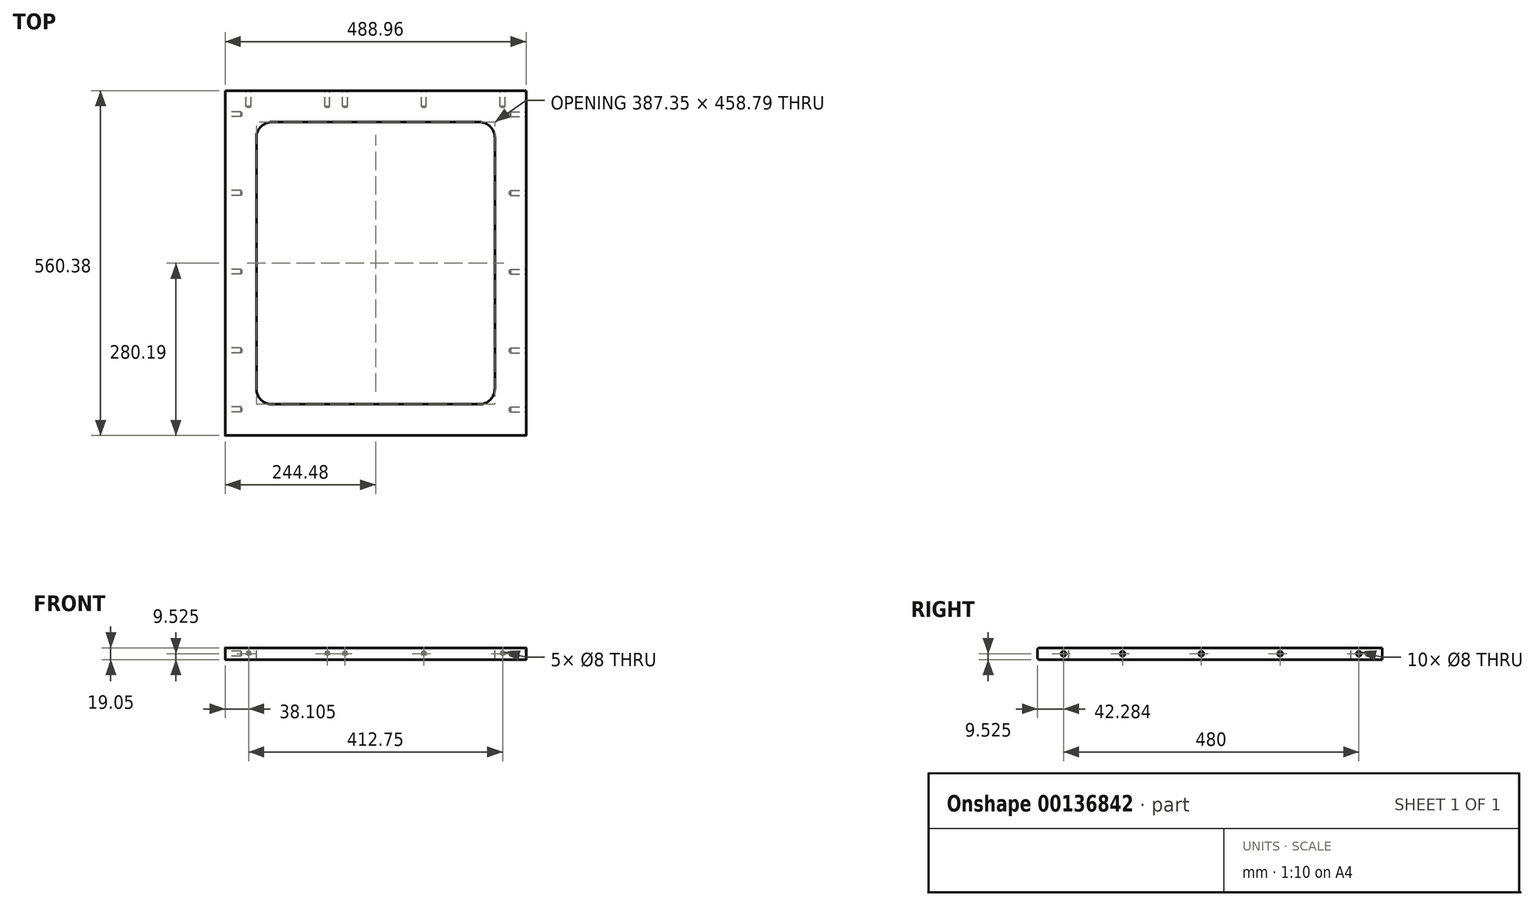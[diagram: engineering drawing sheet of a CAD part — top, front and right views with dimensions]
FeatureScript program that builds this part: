
annotation { "Feature Type Name" : "Feature", "Feature Type Description" : "" }
export const myFeature = defineFeature(function(context is Context, id is Id, definition is map)
    precondition{}
    {
        {
            var Q0;
            Q0=qCreatedBy(makeId("Top.planeOp"),FACE);
            var sketch = newSketch(context, id + "F0", { "sketchPlane" : qUnion([Q0])});
            skLineSegment(sketch, "E0.bottom", {"start": v(244.48, -280.2) * mm, "end": v(-244.47, -280.2) * mm});
            skLineSegment(sketch, "E0.top", {"start": v(244.47, 280.2) * mm, "end": v(-244.48, 280.2) * mm});
            skLineSegment(sketch, "E0.left", {"start": v(244.48, -280.2) * mm, "end": v(244.47, 280.2) * mm});
            skLineSegment(sketch, "E0.right", {"start": v(-244.47, -280.2) * mm, "end": v(-244.48, 280.2) * mm});
            skPoint(sketch, "E0.middle", {"position": v(0, 0) * mm});
            skSolve(sketch);
        }
        {
            var Q0;
            Q0=makeQuery(id+"F0.imprint","IMPRINT",FACE,{"disambiguationData":[TD([[makeQuery(id+"F0.imprint","IMPRINT",EDGE,{"derivedFrom":sQuery(id+"F0.wireOp",EDGE,"E0.bottom")}),-1.0]])]});
            extrude(context, id + "F1", {"entities" : qUnion([Q0]), "oppositeDirection" : true, "depth" : 19.05 * mm});
        }
        {
            var Q0;
            Q0=makeQuery(id+"F1.opExtrude","SWEPT_FACE",FACE,{"disambiguationData":[OSD([sQuery(id+"F0.wireOp",EDGE,"E0.left")])]});
            var sketch = newSketch(context, id + "F2", { "sketchPlane" : qUnion([Q0])});
            skPoint(sketch, "E1", {"position": v(242.1, -9.53) * mm});
            skPoint(sketch, "E2", {"position": v(114.1, -9.53) * mm});
            skPoint(sketch, "E3", {"position": v(-13.9, -9.53) * mm});
            skPoint(sketch, "E4", {"position": v(-141.9, -9.53) * mm});
            skPoint(sketch, "E5", {"position": v(-237.9, -9.53) * mm});
            skSolve(sketch);
        }
        {
            var Q0;
            Q0=qCreatedBy(makeId("Right.planeOp"),FACE);
            var sketch = newSketch(context, id + "F3", { "sketchPlane" : qUnion([Q0])});
            skPoint(sketch, "E6", {"position": v(-271.83, -132.34) * mm});
            skCircle(sketch, "E7", {"center": v(-271.83, -132.34) * mm, "radius": 4 * mm});
            skSolve(sketch);
        }
        {
            var Q0;
            Q0=makeQuery(id+"F3.imprint","IMPRINT",FACE,{"disambiguationData":[TD([[makeQuery(id+"F3.imprint","IMPRINT",EDGE,{"derivedFrom":sQuery(id+"F3.wireOp",EDGE,"E7")}),1.0]])]});
            extrude(context, id + "F4", {"entities" : qUnion([Q0]), "oppositeDirection" : true, "depth" : 26.99 * mm});
        }
        {
            var Q0;
            Q0=makeQuery(id+"F4.opExtrude","CAP_EDGE",EDGE,{"disambiguationData":[OSD([sQuery(id+"F3.wireOp",EDGE,"E7")])],"isStart":false});
            chamfer(context, id + "F5", {"entities" : qUnion([Q0]), "width" : 1.59 * mm, "tangentPropagation" : true});
        }
        {
            var Q0;
            Q0=makeQuery(id+"F4.opExtrude","SWEPT_BODY",BODY,{"disambiguationData":[OSD([sQuery(id+"F3.wireOp",EDGE,"E7")])]});
            var Q1;
            Q1=sQuery(id+"F3.wireOp",VERTEX,"E6");
            var Q2;
            Q2=sQuery(id+"F2.wireOp",VERTEX,"E5");
            transform(context, id + "F6", {"entities" : qUnion([Q0]), "transformType" : TransformType.TRANSLATION_ENTITY, "oppositeDirectionEntity" : false, "transformLine" : qUnion([Q1, Q2]), "makeCopy" : true});
        }
        {
            var Q0;
            Q0=makeQuery(id+"F4.opExtrude","SWEPT_BODY",BODY,{"disambiguationData":[OSD([sQuery(id+"F3.wireOp",EDGE,"E7")])]});
            var Q1;
            Q1=sQuery(id+"F3.wireOp",VERTEX,"E6");
            var Q2;
            Q2=sQuery(id+"F2.wireOp",VERTEX,"E4");
            transform(context, id + "F7", {"entities" : qUnion([Q0]), "transformType" : TransformType.TRANSLATION_ENTITY, "oppositeDirectionEntity" : false, "transformLine" : qUnion([Q1, Q2]), "makeCopy" : true});
        }
        {
            var Q0;
            Q0=makeQuery(id+"F4.opExtrude","SWEPT_BODY",BODY,{"disambiguationData":[OSD([sQuery(id+"F3.wireOp",EDGE,"E7")])]});
            var Q1;
            Q1=sQuery(id+"F3.wireOp",VERTEX,"E6");
            var Q2;
            Q2=sQuery(id+"F2.wireOp",VERTEX,"E3");
            transform(context, id + "F8", {"entities" : qUnion([Q0]), "transformType" : TransformType.TRANSLATION_ENTITY, "oppositeDirectionEntity" : false, "transformLine" : qUnion([Q1, Q2]), "makeCopy" : true});
        }
        {
            var Q0;
            Q0=makeQuery(id+"F4.opExtrude","SWEPT_BODY",BODY,{"disambiguationData":[OSD([sQuery(id+"F3.wireOp",EDGE,"E7")])]});
            var Q1;
            Q1=sQuery(id+"F3.wireOp",VERTEX,"E6");
            var Q2;
            Q2=sQuery(id+"F2.wireOp",VERTEX,"E2");
            transform(context, id + "F9", {"entities" : qUnion([Q0]), "transformType" : TransformType.TRANSLATION_ENTITY, "oppositeDirectionEntity" : false, "transformLine" : qUnion([Q1, Q2]), "makeCopy" : true});
        }
        {
            var Q0;
            Q0=makeQuery(id+"F4.opExtrude","SWEPT_BODY",BODY,{"disambiguationData":[OSD([sQuery(id+"F3.wireOp",EDGE,"E7")])]});
            var Q1;
            Q1=sQuery(id+"F3.wireOp",VERTEX,"E6");
            var Q2;
            Q2=sQuery(id+"F2.wireOp",VERTEX,"E1");
            transform(context, id + "F10", {"entities" : qUnion([Q0]), "transformType" : TransformType.TRANSLATION_ENTITY, "oppositeDirectionEntity" : false, "transformLine" : qUnion([Q1, Q2]), "makeCopy" : true});
        }
        {
            var Q0;
            Q0=makeQuery(id+"F6.opPattern","COPY",BODY,{"derivedFrom":makeQuery(id+"F4.opExtrude","SWEPT_BODY",BODY,{"disambiguationData":[OSD([sQuery(id+"F3.wireOp",EDGE,"E7")])]}),"instanceName":"1"});
            var Q1;
            Q1=makeQuery(id+"F7.opPattern","COPY",BODY,{"derivedFrom":makeQuery(id+"F4.opExtrude","SWEPT_BODY",BODY,{"disambiguationData":[OSD([sQuery(id+"F3.wireOp",EDGE,"E7")])]}),"instanceName":"1"});
            var Q2;
            Q2=makeQuery(id+"F8.opPattern","COPY",BODY,{"derivedFrom":makeQuery(id+"F4.opExtrude","SWEPT_BODY",BODY,{"disambiguationData":[OSD([sQuery(id+"F3.wireOp",EDGE,"E7")])]}),"instanceName":"1"});
            var Q3;
            Q3=makeQuery(id+"F9.opPattern","COPY",BODY,{"derivedFrom":makeQuery(id+"F4.opExtrude","SWEPT_BODY",BODY,{"disambiguationData":[OSD([sQuery(id+"F3.wireOp",EDGE,"E7")])]}),"instanceName":"1"});
            var Q4;
            Q4=makeQuery(id+"F10.opPattern","COPY",BODY,{"derivedFrom":makeQuery(id+"F4.opExtrude","SWEPT_BODY",BODY,{"disambiguationData":[OSD([sQuery(id+"F3.wireOp",EDGE,"E7")])]}),"instanceName":"1"});
            var Q5;
            Q5=qCreatedBy(makeId("Right.planeOp"),FACE);
            mirror(context, id + "F11", {"entities" : qUnion([Q0, Q1, Q2, Q3, Q4]), "mirrorPlane" : qUnion([Q5])});
        }
        {
            var Q0;
            Q0=makeQuery(id+"F11.opPattern","COPY",BODY,{"derivedFrom":makeQuery(id+"F6.opPattern","COPY",BODY,{"derivedFrom":makeQuery(id+"F4.opExtrude","SWEPT_BODY",BODY,{"disambiguationData":[OSD([sQuery(id+"F3.wireOp",EDGE,"E7")])]}),"instanceName":"1"}),"instanceName":"1"});
            var Q1;
            Q1=makeQuery(id+"F11.opPattern","COPY",BODY,{"derivedFrom":makeQuery(id+"F7.opPattern","COPY",BODY,{"derivedFrom":makeQuery(id+"F4.opExtrude","SWEPT_BODY",BODY,{"disambiguationData":[OSD([sQuery(id+"F3.wireOp",EDGE,"E7")])]}),"instanceName":"1"}),"instanceName":"1"});
            var Q2;
            Q2=makeQuery(id+"F11.opPattern","COPY",BODY,{"derivedFrom":makeQuery(id+"F8.opPattern","COPY",BODY,{"derivedFrom":makeQuery(id+"F4.opExtrude","SWEPT_BODY",BODY,{"disambiguationData":[OSD([sQuery(id+"F3.wireOp",EDGE,"E7")])]}),"instanceName":"1"}),"instanceName":"1"});
            var Q3;
            Q3=makeQuery(id+"F11.opPattern","COPY",BODY,{"derivedFrom":makeQuery(id+"F9.opPattern","COPY",BODY,{"derivedFrom":makeQuery(id+"F4.opExtrude","SWEPT_BODY",BODY,{"disambiguationData":[OSD([sQuery(id+"F3.wireOp",EDGE,"E7")])]}),"instanceName":"1"}),"instanceName":"1"});
            var Q4;
            Q4=makeQuery(id+"F11.opPattern","COPY",BODY,{"derivedFrom":makeQuery(id+"F10.opPattern","COPY",BODY,{"derivedFrom":makeQuery(id+"F4.opExtrude","SWEPT_BODY",BODY,{"disambiguationData":[OSD([sQuery(id+"F3.wireOp",EDGE,"E7")])]}),"instanceName":"1"}),"instanceName":"1"});
            var Q5;
            Q5=makeQuery(id+"F10.opPattern","COPY",BODY,{"derivedFrom":makeQuery(id+"F4.opExtrude","SWEPT_BODY",BODY,{"disambiguationData":[OSD([sQuery(id+"F3.wireOp",EDGE,"E7")])]}),"instanceName":"1"});
            var Q6;
            Q6=makeQuery(id+"F9.opPattern","COPY",BODY,{"derivedFrom":makeQuery(id+"F4.opExtrude","SWEPT_BODY",BODY,{"disambiguationData":[OSD([sQuery(id+"F3.wireOp",EDGE,"E7")])]}),"instanceName":"1"});
            var Q7;
            Q7=makeQuery(id+"F8.opPattern","COPY",BODY,{"derivedFrom":makeQuery(id+"F4.opExtrude","SWEPT_BODY",BODY,{"disambiguationData":[OSD([sQuery(id+"F3.wireOp",EDGE,"E7")])]}),"instanceName":"1"});
            var Q8;
            Q8=makeQuery(id+"F7.opPattern","COPY",BODY,{"derivedFrom":makeQuery(id+"F4.opExtrude","SWEPT_BODY",BODY,{"disambiguationData":[OSD([sQuery(id+"F3.wireOp",EDGE,"E7")])]}),"instanceName":"1"});
            var Q9;
            Q9=makeQuery(id+"F6.opPattern","COPY",BODY,{"derivedFrom":makeQuery(id+"F4.opExtrude","SWEPT_BODY",BODY,{"disambiguationData":[OSD([sQuery(id+"F3.wireOp",EDGE,"E7")])]}),"instanceName":"1"});
            var Q10;
            Q10=makeQuery(id+"F1.opExtrude","SWEPT_BODY",BODY,{"disambiguationData":[OSD([sQuery(id+"F0.wireOp",EDGE,"E0.bottom"),sQuery(id+"F0.wireOp",EDGE,"E0.top"),sQuery(id+"F0.wireOp",EDGE,"E0.left"),sQuery(id+"F0.wireOp",EDGE,"E0.right")])]});
            booleanBodies(context, id + "F12", {"operationType" : BooleanOperationType.SUBTRACTION, "tools" : qUnion([Q0, Q1, Q2, Q3, Q4, Q5, Q6, Q7, Q8, Q9]), "targets" : qUnion([Q10])});
        }
        {
            var Q0;
            Q0=makeQuery(id+"F4.opExtrude","SWEPT_BODY",BODY,{"disambiguationData":[OSD([sQuery(id+"F3.wireOp",EDGE,"E7")])]});
            var Q1;
            Q1=makeQuery(id+"F1.opExtrude","SWEPT_EDGE",EDGE,{"disambiguationData":[OSD([sQuery(id+"F0.wireOp",EDGE,"E0.bottom"),sQuery(id+"F0.wireOp",EDGE,"E0.left")])]});
            transform(context, id + "F13", {"entities" : qUnion([Q0]), "transformType" : TransformType.ROTATION, "transformAxis" : qUnion([Q1]), "angle" : 90 * degree, "makeCopy" : false});
        }
        {
            var Q0;
            Q0=makeQuery(id+"F4.opExtrude","CAP_FACE",FACE,{"disambiguationData":[OSD([sQuery(id+"F3.wireOp",EDGE,"E7")])],"isStart":true});
            var sketch = newSketch(context, id + "F14", { "sketchPlane" : qUnion([Q0])});
            skPoint(sketch, "E8", {"position": v(-236.1, -132.34) * mm});
            skSolve(sketch);
        }
        {
            var Q0;
            Q0=makeQuery(id+"F1.opExtrude","SWEPT_FACE",FACE,{"disambiguationData":[OSD([sQuery(id+"F0.wireOp",EDGE,"E0.top")])]});
            var sketch = newSketch(context, id + "F15", { "sketchPlane" : qUnion([Q0])});
            skPoint(sketch, "E9", {"position": v(-206.38, -9.53) * mm});
            skPoint(sketch, "E10", {"position": v(-78.38, -9.53) * mm});
            skPoint(sketch, "E11", {"position": v(49.62, -9.53) * mm});
            skPoint(sketch, "E12", {"position": v(78.38, -9.53) * mm});
            skPoint(sketch, "E13", {"position": v(206.38, -9.53) * mm});
            skSolve(sketch);
        }
        {
            var Q0;
            Q0=makeQuery(id+"F4.opExtrude","SWEPT_BODY",BODY,{"disambiguationData":[OSD([sQuery(id+"F3.wireOp",EDGE,"E7")])]});
            var Q1;
            Q1=sQuery(id+"F14.wireOp",VERTEX,"E8");
            var Q2;
            Q2=sQuery(id+"F15.wireOp",VERTEX,"E13");
            transform(context, id + "F16", {"entities" : qUnion([Q0]), "transformType" : TransformType.TRANSLATION_ENTITY, "oppositeDirectionEntity" : false, "transformLine" : qUnion([Q1, Q2]), "makeCopy" : true});
        }
        {
            var Q0;
            Q0=makeQuery(id+"F4.opExtrude","SWEPT_BODY",BODY,{"disambiguationData":[OSD([sQuery(id+"F3.wireOp",EDGE,"E7")])]});
            var Q1;
            Q1=sQuery(id+"F14.wireOp",VERTEX,"E8");
            var Q2;
            Q2=sQuery(id+"F15.wireOp",VERTEX,"E12");
            transform(context, id + "F17", {"entities" : qUnion([Q0]), "transformType" : TransformType.TRANSLATION_ENTITY, "oppositeDirectionEntity" : false, "transformLine" : qUnion([Q1, Q2]), "makeCopy" : true});
        }
        {
            var Q0;
            Q0=makeQuery(id+"F4.opExtrude","SWEPT_BODY",BODY,{"disambiguationData":[OSD([sQuery(id+"F3.wireOp",EDGE,"E7")])]});
            var Q1;
            Q1=sQuery(id+"F14.wireOp",VERTEX,"E8");
            var Q2;
            Q2=sQuery(id+"F15.wireOp",VERTEX,"E11");
            transform(context, id + "F18", {"entities" : qUnion([Q0]), "transformType" : TransformType.TRANSLATION_ENTITY, "oppositeDirectionEntity" : false, "transformLine" : qUnion([Q1, Q2]), "makeCopy" : true});
        }
        {
            var Q0;
            Q0=makeQuery(id+"F4.opExtrude","SWEPT_BODY",BODY,{"disambiguationData":[OSD([sQuery(id+"F3.wireOp",EDGE,"E7")])]});
            var Q1;
            Q1=sQuery(id+"F14.wireOp",VERTEX,"E8");
            var Q2;
            Q2=sQuery(id+"F15.wireOp",VERTEX,"E10");
            transform(context, id + "F19", {"entities" : qUnion([Q0]), "transformType" : TransformType.TRANSLATION_ENTITY, "oppositeDirectionEntity" : false, "transformLine" : qUnion([Q1, Q2]), "makeCopy" : true});
        }
        {
            var Q0;
            Q0=makeQuery(id+"F4.opExtrude","SWEPT_BODY",BODY,{"disambiguationData":[OSD([sQuery(id+"F3.wireOp",EDGE,"E7")])]});
            var Q1;
            Q1=sQuery(id+"F14.wireOp",VERTEX,"E8");
            var Q2;
            Q2=sQuery(id+"F15.wireOp",VERTEX,"E9");
            transform(context, id + "F20", {"entities" : qUnion([Q0]), "transformType" : TransformType.TRANSLATION_ENTITY, "oppositeDirectionEntity" : false, "transformLine" : qUnion([Q1, Q2]), "makeCopy" : false});
        }
        {
            var Q0;
            Q0=makeQuery(id+"F16.opPattern","COPY",BODY,{"derivedFrom":makeQuery(id+"F4.opExtrude","SWEPT_BODY",BODY,{"disambiguationData":[OSD([sQuery(id+"F3.wireOp",EDGE,"E7")])]}),"instanceName":"1"});
            var Q1;
            Q1=makeQuery(id+"F17.opPattern","COPY",BODY,{"derivedFrom":makeQuery(id+"F4.opExtrude","SWEPT_BODY",BODY,{"disambiguationData":[OSD([sQuery(id+"F3.wireOp",EDGE,"E7")])]}),"instanceName":"1"});
            var Q2;
            Q2=makeQuery(id+"F18.opPattern","COPY",BODY,{"derivedFrom":makeQuery(id+"F4.opExtrude","SWEPT_BODY",BODY,{"disambiguationData":[OSD([sQuery(id+"F3.wireOp",EDGE,"E7")])]}),"instanceName":"1"});
            var Q3;
            Q3=makeQuery(id+"F19.opPattern","COPY",BODY,{"derivedFrom":makeQuery(id+"F4.opExtrude","SWEPT_BODY",BODY,{"disambiguationData":[OSD([sQuery(id+"F3.wireOp",EDGE,"E7")])]}),"instanceName":"1"});
            var Q4;
            Q4=makeQuery(id+"F4.opExtrude","SWEPT_BODY",BODY,{"disambiguationData":[OSD([sQuery(id+"F3.wireOp",EDGE,"E7")])]});
            var Q5;
            Q5=makeQuery(id+"F1.opExtrude","SWEPT_BODY",BODY,{"disambiguationData":[OSD([sQuery(id+"F0.wireOp",EDGE,"E0.bottom"),sQuery(id+"F0.wireOp",EDGE,"E0.top"),sQuery(id+"F0.wireOp",EDGE,"E0.left"),sQuery(id+"F0.wireOp",EDGE,"E0.right")])]});
            booleanBodies(context, id + "F21", {"operationType" : BooleanOperationType.SUBTRACTION, "tools" : qUnion([Q0, Q1, Q2, Q3, Q4]), "targets" : qUnion([Q5])});
        }
        {
            var Q0;
            Q0=makeQuery(id+"F1.opExtrude","CAP_FACE",FACE,{"disambiguationData":[OSD([sQuery(id+"F0.wireOp",EDGE,"E0.bottom"),sQuery(id+"F0.wireOp",EDGE,"E0.top"),sQuery(id+"F0.wireOp",EDGE,"E0.left"),sQuery(id+"F0.wireOp",EDGE,"E0.right")])],"isStart":true});
            var sketch = newSketch(context, id + "F22", { "sketchPlane" : qUnion([Q0])});
            skLineSegment(sketch, "E14.0", {"start": v(-193.67, -204) * mm, "end": v(-193.68, 204) * mm});
            skLineSegment(sketch, "E15.0", {"start": v(168.27, 229.4) * mm, "end": v(-168.28, 229.4) * mm});
            skLineSegment(sketch, "E16.0", {"start": v(193.68, -204) * mm, "end": v(193.67, 204) * mm});
            skLineSegment(sketch, "E17.0", {"start": v(168.28, -229.4) * mm, "end": v(-168.27, -229.4) * mm});
            skArc(sketch, "E18.filletArc", {"start": v(-168.28, 229.4) * mm, "mid": v(-186.24, 221.95) * mm, "end": v(-193.68, 204) * mm});
            skArc(sketch, "E19.filletArc", {"start": v(193.68, 204) * mm, "mid": v(186.24, 221.95) * mm, "end": v(168.27, 229.4) * mm});
            skArc(sketch, "E20.filletArc", {"start": v(168.28, -229.4) * mm, "mid": v(186.24, -221.95) * mm, "end": v(193.68, -204) * mm});
            skArc(sketch, "E21.filletArc", {"start": v(-193.67, -204) * mm, "mid": v(-186.24, -221.95) * mm, "end": v(-168.27, -229.4) * mm});
            skSolve(sketch);
        }
        {
            var Q0;
            Q0=makeQuery(id+"F22.imprint","IMPRINT",FACE,{"disambiguationData":[TD([[makeQuery(id+"F22.imprint","IMPRINT",EDGE,{"derivedFrom":sQuery(id+"F22.wireOp",EDGE,"E14.0")}),-1.0]])]});
            extrude(context, id + "F23", {"entities" : qUnion([Q0]), "operationType" : NewBodyOperationType.REMOVE, "endBound" : BoundingType.THROUGH_ALL, "oppositeDirection" : true, "depth" : 25.4 * mm});
        }
        {
            var Q0;
            Q0=makeQuery(id+"F1.opExtrude","CAP_EDGE",EDGE,{"disambiguationData":[OSD([sQuery(id+"F0.wireOp",EDGE,"E0.bottom")])],"isStart":true});
            var Q1;
            Q1=makeQuery(id+"F1.opExtrude","CAP_EDGE",EDGE,{"disambiguationData":[OSD([sQuery(id+"F0.wireOp",EDGE,"E0.bottom")])],"isStart":false});
            fillet(context, id + "F24", {"entities" : qUnion([Q0, Q1]), "radius" : 3.17 * mm, "tangentPropagation" : true, "allowEdgeOverflow" : false});
        }
    });
